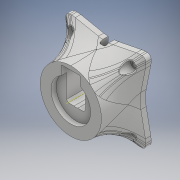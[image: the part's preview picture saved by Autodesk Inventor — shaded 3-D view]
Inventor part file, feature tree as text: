
AUTODESK INVENTOR PART (.ipt)
format: ipt  version: 2018 (Build 220112000, 112)  size: 1,921,024 bytes
history: native  units: mm
features: sketch x37, projected_geometry x36, extrude x32, fillet x12, hole x4, chamfer x4, mirror x1, other x1, revolve x1, shell x1, pattern_circular x1
ambient origin geometry x8: Origin, YZ Plane, XZ Plane, XY Plane, X Axis, Y Axis, Z Axis, Center Point
bodies: Solid1 (feature_tree)
feature tree (130):
  extrude  "Extrusion1"  Depth=45.0mm
  extrude  "Extrusion2"  Depth=1.95mm
  hole  "Hole1"  [1 undecoded]
  hole  "Hole2"  [1 undecoded]
  fillet  "Fillet1"  Radius=14.0mm
  extrude  "Extrusion3"  Depth=18.5mm
  extrude  "Extrusion4"  Depth=10.0mm
  extrude  "Extrusion5"  Depth=2.0mm
  extrude  "Extrusion6"  Depth=8.0mm
  hole  "Hole3"  [1 undecoded]
  extrude  "Extrusion7"  Depth=0.5mm
  extrude  "Extrusion8"  Depth=5.0mm TaperAngle=0.0deg
  extrude  "Extrusion9"  Depth=10.0mm
  extrude  "Extrusion10"  Depth=10.0mm
  extrude  "Extrusion11"  Depth=14.5mm
  extrude  "Extrusion12"  Depth=20.0mm
  extrude  "Extrusion13"  Depth=5.0mm
  extrude  "Extrusion14"  Depth=5.0mm
  extrude  "Extrusion15"  Depth=5.0mm
  extrude  "Extrusion16"  Depth=5.0mm
  extrude  "Extrusion17"  Depth=4.0mm
  chamfer  "Chamfer1"  Distance=1.0mm
  fillet  "Fillet7"  Radius=20.7mm
  fillet  "Fillet8"  Radius=32.0mm
  mirror  "Mirror1"
  extrude  "Extrusion18"  Depth=5.0mm TaperAngle=0.0deg
  extrude  "Extrusion19"  Depth=8.0mm
  extrude  "Extrusion20"  Depth=0.2mm TaperAngle=0.0deg
  extrude  "Extrusion21"  Depth=0.5mm TaperAngle=0.0deg
  extrude  "Extrusion22"  Depth=3.0mm TaperAngle=0.0deg
  extrude  "Extrusion23"  Depth=5.0mm TaperAngle=0.0deg
  extrude  "Extrusion24"  Depth=2.5mm TaperAngle=45.0deg
  sketch  "Sketch35"  dims[d91=8.0mm d92=0.0mm d93=3.0mm d94=0.0mm]
  other  "Work Axis1"
  revolve  "Revolution1"  [1 undecoded]
  extrude  "Extrusion25"  Depth=4.0mm TaperAngle=0.0deg
  extrude  "Extrusion26"  Depth=19.2mm TaperAngle=0.0deg
  shell  "Shell1"  Thickness=52.1mm
  extrude  "Extrusion27"  Depth=9.0mm
  extrude  "Extrusion28"  Depth=25.0mm
  chamfer  "Chamfer4"  Distance=6.9mm
  chamfer  "Chamfer5"  Distance=5.2mm
  extrude  "Extrusion29"  Depth=2.0mm
  pattern_circular  "Circular Pattern1"  [2 undecoded]
  fillet  "Fillet11"  Radius=5.0mm
  fillet  "Fillet12"  [1 undecoded]
  fillet  "Fillet13"  Radius=5.0mm
  fillet  "Fillet14"  Radius=105.0mm
  chamfer  "Chamfer6"  Distance=105.0mm
  hole  "Hole6"  [1 undecoded]
  extrude  "Extrusion30"  Depth=2.0mm
  fillet  "Fillet15"  Radius=12.8mm
  extrude  "Extrusion31"  Depth=2.0mm
  fillet  "Fillet16"  Radius=12.8mm
  extrude  "Extrusion32"  Depth=20.0mm
  fillet  "Fillet17"  Radius=20.0mm
  fillet  "Fillet18"  Radius=20.0mm
  fillet  "Fillet19"  Radius=6.0mm
  sketch  "Sketch1"  dims[d0=24.5mm d1=45.0mm]
  sketch  "Sketch2"  dims[d2=1.95mm d3=0.0mm d4=2.25mm]
  projected_geometry  "Projected Loop1"
  sketch  "Sketch3"  dims[d5=20.0mm d6=2.25mm]
  projected_geometry  "Projected Loop2"
  sketch  "Sketch4"  dims[d7=5.25mm d8=5.25mm d9=14.0mm]
  projected_geometry  "Projected Loop3"
  sketch  "Sketch5"  dims[d10=5.25mm d11=18.5mm]
  projected_geometry  "Projected Loop4"
  sketch  "Sketch6"  dims[d12=10.0mm d13=0.0mm d14=20.5mm]
  projected_geometry  "Projected Loop5"
  sketch  "Sketch7"  dims[d15=2.0mm d16=2.195mm]
  projected_geometry  "Projected Loop6"
  sketch  "Sketch8"  dims[d17=2.0mm]
  projected_geometry  "Projected Loop7"
  sketch  "Sketch9"  dims[d18=2.4mm d19=6.0mm d20=4.4mm d21=2.0mm d22=90.0deg d23=8.0mm d24=20.594885mm d25=20.5mm]
  projected_geometry  "Projected Loop8"
  projected_geometry  "Projected Loop9"
  sketch  "Sketch10"  dims[d26=26.65mm d27=2.0mm]
  projected_geometry  "Projected Loop10"
  projected_geometry  "Projected Loop11"
  sketch  "Sketch11"  dims[d28=2.0mm]
  projected_geometry  "Projected Loop12"
  sketch  "Sketch12"  dims[d29=2.4mm d30=6.0mm d31=4.4mm d32=2.0mm d33=90.0deg d34=8.0mm d35=20.594885mm d36=0.5mm]
  sketch  "Sketch13"  dims[d37=18.0mm d38=5.0mm d39=0.0mm]
  sketch  "Sketch14"  dims[d41=10.0mm d42=0.0mm d43=24.5mm]
  projected_geometry  "Projected Loop13"
  sketch  "Sketch15"  dims[d44=1.15mm d45=0.0mm d46=10.0mm]
  sketch  "Sketch16"  dims[d47=21.0mm d48=14.5mm]
  projected_geometry  "Projected Loop14"
  sketch  "Sketch17"  dims[d49=20.0mm d50=14.5mm]
  projected_geometry  "Projected Loop15"
  sketch  "Sketch18"  dims[d51=24.5mm d52=5.0mm]
  projected_geometry  "Projected Loop16"
  sketch  "Sketch19"  dims[d53=5.0mm d54=2.25mm]
  projected_geometry  "Projected Loop17"
  sketch  "Sketch20"  dims[d55=2.25mm d56=5.0mm]
  projected_geometry  "Projected Loop18"
  sketch  "Sketch22"  dims[d57=5.0mm d58=9.0mm]
  sketch  "Sketch25"  dims[d59=14.75mm d60=4.0mm d61=1.0mm d62=0.0mm d63=20.7mm]
  sketch  "Sketch27"  dims[d64=2.4mm d65=6.0mm d66=4.4mm d67=2.0mm d68=90.0deg d69=8.0mm d70=20.594885mm d72=32.0mm]
  projected_geometry  "Projected Loop22"
  sketch  "Sketch28"  dims[d73=5.0mm d74=0.0mm d75=1.0mm d76=0.0mm]
  projected_geometry  "Projected Loop23"
  sketch  "Sketch29"  dims[d77=12.25mm d78=0.0mm d80=8.0mm]
  projected_geometry  "Projected Loop24"
  sketch  "Sketch30"  dims[d81=4.5mm d82=0.0mm d84=0.2mm d85=0.0mm]
  projected_geometry  "Projected Loop25"
  sketch  "Sketch33"  dims[d86=21.0mm d87=0.5mm d88=0.0mm]
  projected_geometry  "Projected Loop26"
  sketch  "Sketch36"  dims[d95=5.0mm d96=0.0mm d98=0.2mm d99=0.0mm]
  projected_geometry  "Projected Loop27"
  sketch  "Sketch37"  dims[d100=0.2mm d101=0.0mm d102=2.5mm d103=2.0mm d104=45.0deg]
  projected_geometry  "Projected Loop28"
  sketch  "Sketch38"  dims[d105=1.5mm d114=0.5mm]
  projected_geometry  "Projected Loop29"
  projected_geometry  "Projected Loop30"
  projected_geometry  "Projected Loop31"
  projected_geometry  "Projected Loop32"
  sketch  "Sketch39"  dims[d115=22.55mm d116=0.0mm d128=4.0mm d129=0.0mm]
  projected_geometry  "Projected Loop33"
  projected_geometry  "Projected Loop34"
  sketch  "Sketch40"  dims[d130=4.0mm d131=0.0mm d132=19.2mm d133=0.0mm d134=52.1mm]
  projected_geometry  "Projected Loop35"
  sketch  "Sketch41"  dims[d135=6.8mm d136=0.0mm d137=9.0mm]
  projected_geometry  "Projected Loop36"
  sketch  "Sketch42"  dims[d138=9.0mm d139=25.0mm d140=6.9mm d141=0.0mm]
  sketch  "Sketch43"  dims[d142=5.2mm]
  projected_geometry  "Projected Loop37"
  sketch  "Sketch44"  dims[d143=5.2mm d144=5.2mm d145=5.2mm d146=2.5mm d147=0.0mm d148=5.0mm d149=90.0deg d150=5.0mm d151=105.0mm d152=105.0mm d153=5.0mm d154=0.0mm d156=12.8mm d157=12.8mm d158=12.8mm d159=12.8mm d160=20.0mm d161=20.0mm d162=20.0mm d163=6.0mm d164=40.0mm d165=0.0mm d166=8.0mm d167=40.0mm d168=0.0mm d169=40.0mm d170=0.0mm d178=5.1mm d179=2.45mm d180=45.0deg d181=4.1mm d182=2.45mm d183=45.0deg d184=10.0mm d185=10.0mm d186=40.0mm d187=0.0mm d188=40.0mm d189=360.0deg d191=5.1mm d192=25.0mm d193=50.0mm d194=50.0mm d195=5.0mm d196=2.0mm d197=45.0deg d198=110.0mm d199=77.781746mm d200=77.781746mm d201=6.4mm d202=6.0mm d203=12.6mm d204=2.0mm d205=90.0deg d206=8.0mm d207=20.594885mm d208=11.0mm d209=11.0mm d210=11.0mm d211=11.0mm d212=45.0mm d213=0.0mm d214=1.0mm d215=2.0mm d216=0.0mm d217=1.5mm d218=8.0mm d219=12.0mm d220=12.0mm d221=0.0mm d222=2.0mm d223=5.0mm d224=2.0mm]
  projected_geometry  "Projected Loop38"
  projected_geometry  "Project Cut Edges1"
note: 8 required parameter values undecoded (feature->parameter linkage not recoverable at this tier; creation-order binding heuristic only, values carry confidence <= 0.55)